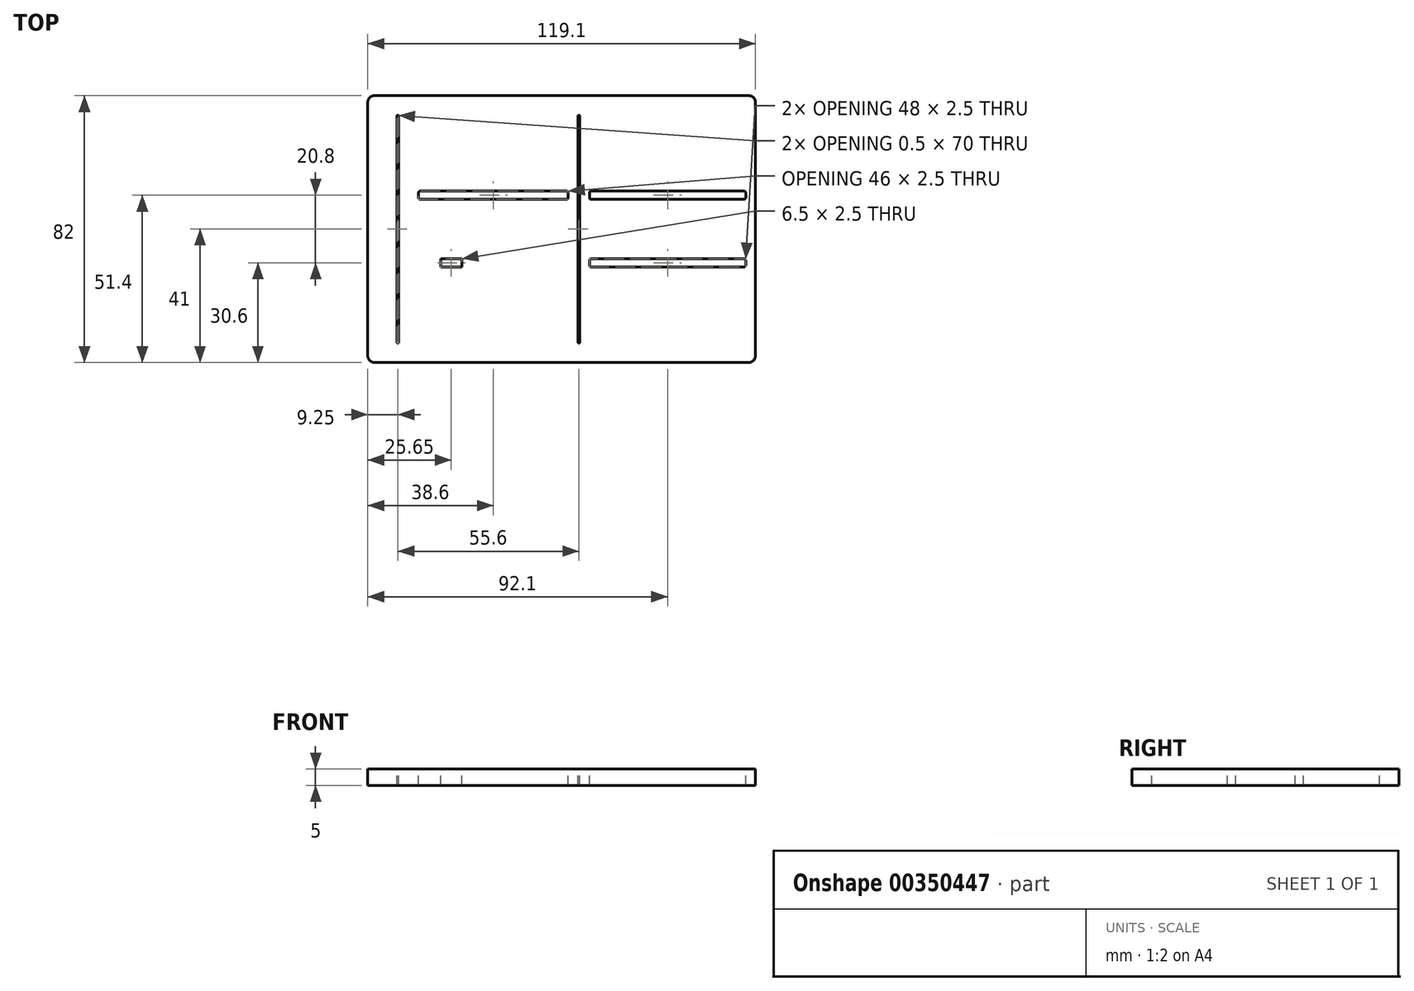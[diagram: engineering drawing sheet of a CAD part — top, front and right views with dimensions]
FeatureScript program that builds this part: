
annotation { "Feature Type Name" : "Feature", "Feature Type Description" : "" }
export const myFeature = defineFeature(function(context is Context, id is Id, definition is map)
    precondition{}
    {
        {
            var Q0;
            Q0=qCreatedBy(makeId("Top.planeOp"),FACE);
            var sketch = newSketch(context, id + "F0", { "sketchPlane" : qUnion([Q0])});
            skLineSegment(sketch, "E0.bottom", {"start": v(0, 0) * mm, "end": v(119.1, 0) * mm});
            skLineSegment(sketch, "E0.top", {"start": v(0, 82) * mm, "end": v(119.1, 82) * mm});
            skLineSegment(sketch, "E0.left", {"start": v(0, 0) * mm, "end": v(0, 82) * mm});
            skLineSegment(sketch, "E0.right", {"start": v(119.1, 0) * mm, "end": v(119.1, 82) * mm});
            skSolve(sketch);
        }
        {
            var Q0;
            Q0=qSketchRegion(id+"F0",true);
            extrude(context, id + "F1", {"entities" : qUnion([Q0]), "depth" : 5 * mm});
        }
        {
            var Q0;
            Q0=makeQuery(id+"F1.opExtrude","CAP_FACE",FACE,{"disambiguationData":[OSD([sQuery(id+"F0.wireOp",EDGE,"E0.bottom"),sQuery(id+"F0.wireOp",EDGE,"E0.top"),sQuery(id+"F0.wireOp",EDGE,"E0.left"),sQuery(id+"F0.wireOp",EDGE,"E0.right")])],"isStart":false});
            var sketch = newSketch(context, id + "F2", { "sketchPlane" : qUnion([Q0])});
            skLineSegment(sketch, "E1", {"start": v(64.6, 25) * mm, "end": v(64.6, 76) * mm});
            skLineSegment(sketch, "E2", {"start": v(64.6, 25) * mm, "end": v(64.6, 6) * mm});
            skLineSegment(sketch, "E3", {"start": v(64.6, 76) * mm, "end": v(65.1, 76) * mm});
            skLineSegment(sketch, "E4", {"start": v(65.1, 76) * mm, "end": v(65.1, 6) * mm});
            skLineSegment(sketch, "E5", {"start": v(65.1, 6) * mm, "end": v(64.6, 6) * mm});
            skSolve(sketch);
        }
        {
            var Q0;
            Q0=qSketchRegion(id+"F2",true);
            extrude(context, id + "F3", {"entities" : qUnion([Q0]), "operationType" : NewBodyOperationType.REMOVE, "oppositeDirection" : true, "depth" : 63.1 * mm});
        }
        {
            var Q0;
            Q0=makeQuery(id+"F1.opExtrude","CAP_FACE",FACE,{"disambiguationData":[OSD([sQuery(id+"F0.wireOp",EDGE,"E0.bottom"),sQuery(id+"F0.wireOp",EDGE,"E0.top"),sQuery(id+"F0.wireOp",EDGE,"E0.left"),sQuery(id+"F0.wireOp",EDGE,"E0.right")])],"isStart":false});
            var sketch = newSketch(context, id + "F4", { "sketchPlane" : qUnion([Q0])});
            skLineSegment(sketch, "E6", {"start": v(38.92, 50.15) * mm, "end": v(61.6, 50.15) * mm});
            skLineSegment(sketch, "E7", {"start": v(38.92, 50.15) * mm, "end": v(38.92, 31.85) * mm});
            skPoint(sketch, "E7.endSnap0", {"position": v(38.92, 41) * mm});
            skLineSegment(sketch, "E8", {"start": v(38.92, 50.15) * mm, "end": v(15.6, 50.15) * mm});
            skLineSegment(sketch, "E9", {"start": v(15.6, 31.85) * mm, "end": v(61.6, 31.85) * mm});
            skLineSegment(sketch, "E10.bottom", {"start": v(15.6, 50.15) * mm, "end": v(61.6, 50.15) * mm});
            skLineSegment(sketch, "E10.top", {"start": v(15.6, 52.65) * mm, "end": v(61.6, 52.65) * mm});
            skLineSegment(sketch, "E10.left", {"start": v(15.6, 50.15) * mm, "end": v(15.6, 52.65) * mm});
            skLineSegment(sketch, "E10.right", {"start": v(61.6, 50.15) * mm, "end": v(61.6, 52.65) * mm});
            skLineSegment(sketch, "E11.top", {"start": v(15.6, 29.35) * mm, "end": v(61.6, 29.35) * mm});
            skLineSegment(sketch, "E11.left", {"start": v(15.6, 31.85) * mm, "end": v(15.6, 29.35) * mm});
            skLineSegment(sketch, "E11.right", {"start": v(61.6, 31.85) * mm, "end": v(61.6, 29.35) * mm});
            skLineSegment(sketch, "E12.bottom", {"start": v(38.92, 31.85) * mm, "end": v(48.1, 31.85) * mm});
            skLineSegment(sketch, "E12.top", {"start": v(38, 29.35) * mm, "end": v(48.1, 29.35) * mm});
            skLineSegment(sketch, "E12.right", {"start": v(48.1, 31.85) * mm, "end": v(48.1, 29.35) * mm});
            skLineSegment(sketch, "E13.bottom", {"start": v(54.6, 31.85) * mm, "end": v(61.6, 31.85) * mm});
            skLineSegment(sketch, "E13.top", {"start": v(54.6, 29.35) * mm, "end": v(61.6, 29.35) * mm});
            skLineSegment(sketch, "E13.left", {"start": v(54.6, 31.85) * mm, "end": v(54.6, 29.35) * mm});
            skLineSegment(sketch, "E14.bottom", {"start": v(15.6, 31.85) * mm, "end": v(22.4, 31.85) * mm});
            skLineSegment(sketch, "E14.top", {"start": v(15.6, 29.35) * mm, "end": v(22.4, 29.35) * mm});
            skLineSegment(sketch, "E14.right", {"start": v(22.4, 31.85) * mm, "end": v(22.4, 29.35) * mm});
            skLineSegment(sketch, "E15.bottom", {"start": v(28.9, 31.85) * mm, "end": v(35.7, 31.85) * mm});
            skLineSegment(sketch, "E15.top", {"start": v(28.9, 29.35) * mm, "end": v(35.7, 29.35) * mm});
            skLineSegment(sketch, "E15.left", {"start": v(28.9, 31.85) * mm, "end": v(28.9, 29.35) * mm});
            skLineSegment(sketch, "E15.right", {"start": v(35.7, 31.85) * mm, "end": v(35.7, 29.35) * mm});
            skLineSegment(sketch, "E16", {"start": v(48.1, 31.85) * mm, "end": v(41.1, 31.85) * mm});
            skLineSegment(sketch, "E17", {"start": v(41.1, 29.35) * mm, "end": v(41.1, 31.85) * mm});
            skLineSegment(sketch, "E18", {"start": v(22.4, 50.15) * mm, "end": v(22.4, 52.65) * mm});
            skLineSegment(sketch, "E19", {"start": v(28.9, 50.15) * mm, "end": v(28.9, 52.65) * mm});
            skLineSegment(sketch, "E20", {"start": v(35.7, 29.35) * mm, "end": v(35.7, 31.85) * mm});
            skLineSegment(sketch, "E21", {"start": v(48.1, 29.35) * mm, "end": v(48.1, 31.85) * mm});
            skLineSegment(sketch, "E22", {"start": v(54.6, 29.35) * mm, "end": v(54.6, 31.85) * mm});
            skLineSegment(sketch, "E23.trimOffspring", {"start": v(35.7, 50.15) * mm, "end": v(35.7, 52.65) * mm});
            skLineSegment(sketch, "E24.trimOffspring", {"start": v(41.1, 50.15) * mm, "end": v(41.1, 52.65) * mm});
            skLineSegment(sketch, "E25.trimOffspring", {"start": v(48.1, 50.15) * mm, "end": v(48.1, 52.65) * mm});
            skLineSegment(sketch, "E26.trimOffspring", {"start": v(54.6, 50.15) * mm, "end": v(54.6, 52.65) * mm});
            skLineSegment(sketch, "E27", {"start": v(38.92, 41) * mm, "end": v(38.92, 31.85) * mm});
            skSolve(sketch);
        }
        {
            var Q0;
            {var subQ0=sQuery(id+"F4.wireOp",EDGE,"E19");Q0=makeQuery(id+"F4.imprint","IMPRINT",FACE,{"disambiguationData":[TD([[makeQuery(id+"F4.imprint","IMPRINT",EDGE,{"derivedFrom":subQ0}),-1.0]])]});}
            var Q1;
            {var subQ0=sQuery(id+"F4.wireOp",EDGE,"E23.trimOffspring");Q1=makeQuery(id+"F4.imprint","IMPRINT",FACE,{"disambiguationData":[TD([[makeQuery(id+"F4.imprint","IMPRINT",EDGE,{"derivedFrom":subQ0}),-1.0]])]});}
            var Q2;
            {var subQ0=sQuery(id+"F4.wireOp",EDGE,"E24.trimOffspring");Q2=makeQuery(id+"F4.imprint","IMPRINT",FACE,{"disambiguationData":[TD([[makeQuery(id+"F4.imprint","IMPRINT",EDGE,{"derivedFrom":subQ0}),-1.0]])]});}
            var Q3;
            {var subQ0=sQuery(id+"F4.wireOp",EDGE,"E25.trimOffspring");Q3=makeQuery(id+"F4.imprint","IMPRINT",FACE,{"disambiguationData":[TD([[makeQuery(id+"F4.imprint","IMPRINT",EDGE,{"derivedFrom":subQ0}),-1.0]])]});}
            var Q4;
            {var subQ0=sQuery(id+"F4.wireOp",EDGE,"E10.left");Q4=makeQuery(id+"F4.imprint","IMPRINT",FACE,{"disambiguationData":[TD([[makeQuery(id+"F4.imprint","IMPRINT",EDGE,{"derivedFrom":subQ0}),-1.0]])]});}
            var Q5;
            {var subQ0=sQuery(id+"F4.wireOp",EDGE,"E18");Q5=makeQuery(id+"F4.imprint","IMPRINT",FACE,{"disambiguationData":[TD([[makeQuery(id+"F4.imprint","IMPRINT",EDGE,{"derivedFrom":subQ0}),-1.0]])]});}
            var Q6;
            {var subQ0=sQuery(id+"F4.wireOp",EDGE,"E10.right");Q6=makeQuery(id+"F4.imprint","IMPRINT",FACE,{"disambiguationData":[TD([[makeQuery(id+"F4.imprint","IMPRINT",EDGE,{"derivedFrom":subQ0}),1.0]])]});}
            var Q7;
            Q7=makeQuery(id+"F4.imprint","IMPRINT",FACE,{"disambiguationData":[TD([[makeQuery(id+"F4.imprint","IMPRINT",EDGE,{"derivedFrom":sQuery(id+"F4.wireOp",EDGE,"E16")}),1.0]])]});
            var Q8;
            Q8=makeQuery(id+"F4.imprint","IMPRINT",FACE,{"disambiguationData":[TD([[makeQuery(id+"F4.imprint","IMPRINT",EDGE,{"derivedFrom":sQuery(id+"F4.wireOp",EDGE,"E15.bottom")}),-1.0]])]});
            var Q9;
            Q9=makeQuery(id+"F4.imprint","IMPRINT",FACE,{"disambiguationData":[TD([[makeQuery(id+"F4.imprint","IMPRINT",EDGE,{"derivedFrom":sQuery(id+"F4.wireOp",EDGE,"E13.bottom")}),-1.0]])]});
            var Q10;
            {var subQ5=sQuery(id+"F4.wireOp",EDGE,"E12.bottom");Q10=makeQuery(id+"F4.imprint","IMPRINT",FACE,{"disambiguationData":[TD([[makeQuery(id+"F4.imprint","IMPRINT",EDGE,{"derivedFrom":subQ5}),-1.0]])]});}
            var Q11;
            {var subQ2=sQuery(id+"F4.wireOp",EDGE,"E21");Q11=makeQuery(id+"F4.imprint","IMPRINT",FACE,{"disambiguationData":[TD([[makeQuery(id+"F4.imprint","IMPRINT",EDGE,{"derivedFrom":subQ2}),-1.0]])]});}
            var Q12;
            {var subQ0=sQuery(id+"F4.wireOp",EDGE,"E14.right");Q12=makeQuery(id+"F4.imprint","IMPRINT",FACE,{"disambiguationData":[TD([[makeQuery(id+"F4.imprint","IMPRINT",EDGE,{"derivedFrom":subQ0}),1.0]])]});}
            var Q13;
            Q13=makeQuery(id+"F4.imprint","IMPRINT",FACE,{"disambiguationData":[TD([[makeQuery(id+"F4.imprint","IMPRINT",EDGE,{"derivedFrom":sQuery(id+"F4.wireOp",EDGE,"E14.bottom")}),-1.0]])]});
            extrude(context, id + "F5", {"entities" : qUnion([Q0, Q1, Q2, Q3, Q4, Q5, Q6, Q7, Q8, Q9, Q10, Q11, Q12, Q13]), "operationType" : NewBodyOperationType.REMOVE, "oppositeDirection" : true, "depth" : 53.3 * mm});
        }
        {
            var Q0;
            Q0=makeQuery(id+"F1.opExtrude","CAP_FACE",FACE,{"disambiguationData":[OSD([sQuery(id+"F0.wireOp",EDGE,"E0.bottom"),sQuery(id+"F0.wireOp",EDGE,"E0.top"),sQuery(id+"F0.wireOp",EDGE,"E0.left"),sQuery(id+"F0.wireOp",EDGE,"E0.right")])],"isStart":false});
            var sketch = newSketch(context, id + "F6", { "sketchPlane" : qUnion([Q0])});
            skLineSegment(sketch, "E28", {"start": v(68.1, 52.65) * mm, "end": v(116.1, 52.65) * mm});
            skLineSegment(sketch, "E29", {"start": v(116.1, 52.65) * mm, "end": v(116.1, 50.15) * mm});
            skLineSegment(sketch, "E30", {"start": v(116.1, 50.15) * mm, "end": v(68.1, 50.15) * mm});
            skLineSegment(sketch, "E31", {"start": v(68.1, 50.15) * mm, "end": v(68.1, 52.65) * mm});
            skLineSegment(sketch, "E32", {"start": v(68.1, 31.85) * mm, "end": v(68.1, 29.35) * mm});
            skLineSegment(sketch, "E33", {"start": v(68.1, 29.35) * mm, "end": v(116.1, 29.35) * mm});
            skLineSegment(sketch, "E34", {"start": v(116.1, 29.35) * mm, "end": v(116.1, 31.85) * mm});
            skLineSegment(sketch, "E35", {"start": v(116.1, 31.85) * mm, "end": v(68.1, 31.85) * mm});
            skSolve(sketch);
        }
        {
            var Q0;
            Q0=makeQuery(id+"F6.imprint","IMPRINT",FACE,{"disambiguationData":[TD([[makeQuery(id+"F6.imprint","IMPRINT",EDGE,{"derivedFrom":sQuery(id+"F6.wireOp",EDGE,"E28")}),-1.0]])]});
            var Q1;
            Q1=makeQuery(id+"F6.imprint","IMPRINT",FACE,{"disambiguationData":[TD([[makeQuery(id+"F6.imprint","IMPRINT",EDGE,{"derivedFrom":sQuery(id+"F6.wireOp",EDGE,"E32")}),1.0]])]});
            extrude(context, id + "F7", {"entities" : qUnion([Q0, Q1]), "operationType" : NewBodyOperationType.REMOVE, "oppositeDirection" : true, "depth" : 27.8 * mm});
        }
        {
            var Q0;
            Q0=makeQuery(id+"F1.opExtrude","CAP_FACE",FACE,{"disambiguationData":[OSD([sQuery(id+"F0.wireOp",EDGE,"E0.bottom"),sQuery(id+"F0.wireOp",EDGE,"E0.top"),sQuery(id+"F0.wireOp",EDGE,"E0.left"),sQuery(id+"F0.wireOp",EDGE,"E0.right")])],"isStart":false});
            var sketch = newSketch(context, id + "F8", { "sketchPlane" : qUnion([Q0])});
            skLineSegment(sketch, "E36.bottom", {"start": v(9, 76) * mm, "end": v(9.5, 76) * mm});
            skLineSegment(sketch, "E36.top", {"start": v(9, 6) * mm, "end": v(9.5, 6) * mm});
            skLineSegment(sketch, "E36.left", {"start": v(9, 76) * mm, "end": v(9, 6) * mm});
            skLineSegment(sketch, "E36.right", {"start": v(9.5, 76) * mm, "end": v(9.5, 6) * mm});
            skSolve(sketch);
        }
        {
            var Q0;
            Q0=makeQuery(id+"F8.imprint","IMPRINT",FACE,{"disambiguationData":[TD([[makeQuery(id+"F8.imprint","IMPRINT",EDGE,{"derivedFrom":sQuery(id+"F8.wireOp",EDGE,"E36.bottom")}),-1.0]])]});
            extrude(context, id + "F9", {"entities" : qUnion([Q0]), "operationType" : NewBodyOperationType.REMOVE, "oppositeDirection" : true, "depth" : 25 * mm});
        }
        {
            var Q0;
            Q0=makeQuery(id+"F1.opExtrude","SWEPT_EDGE",EDGE,{"disambiguationData":[OSD([sQuery(id+"F0.wireOp",EDGE,"E0.bottom"),sQuery(id+"F0.wireOp",EDGE,"E0.right")])]});
            var Q1;
            Q1=makeQuery(id+"F1.opExtrude","SWEPT_EDGE",EDGE,{"disambiguationData":[OSD([sQuery(id+"F0.wireOp",EDGE,"E0.bottom"),sQuery(id+"F0.wireOp",EDGE,"E0.left")])]});
            var Q2;
            Q2=makeQuery(id+"F1.opExtrude","SWEPT_EDGE",EDGE,{"disambiguationData":[OSD([sQuery(id+"F0.wireOp",EDGE,"E0.top"),sQuery(id+"F0.wireOp",EDGE,"E0.right")])]});
            var Q3;
            Q3=makeQuery(id+"F1.opExtrude","SWEPT_EDGE",EDGE,{"disambiguationData":[OSD([sQuery(id+"F0.wireOp",EDGE,"E0.top"),sQuery(id+"F0.wireOp",EDGE,"E0.left")])]});
            fillet(context, id + "F10", {"entities" : qUnion([Q0, Q1, Q2, Q3]), "radius" : 2 * mm, "tangentPropagation" : true, "allowEdgeOverflow" : false});
        }
        {
            var Q0;
            Q0=makeQuery(id+"F5.boolean.opBoolean","COPY",EDGE,{"derivedFrom":makeQuery(id+"F5.opExtrude","SWEPT_EDGE",EDGE,{"disambiguationData":[OSD([sQuery(id+"F4.wireOp",EDGE,"E10.top"),sQuery(id+"F4.wireOp",EDGE,"E10.left")])]})});
            var Q1;
            Q1=makeQuery(id+"F5.boolean.opBoolean","COPY",EDGE,{"derivedFrom":makeQuery(id+"F5.opExtrude","SWEPT_EDGE",EDGE,{"disambiguationData":[OSD([sQuery(id+"F4.wireOp",EDGE,"E10.bottom"),sQuery(id+"F4.wireOp",EDGE,"E10.left")])]})});
            var Q2;
            Q2=makeQuery(id+"F5.boolean.opBoolean","COPY",EDGE,{"derivedFrom":makeQuery(id+"F5.opExtrude","SWEPT_EDGE",EDGE,{"disambiguationData":[OSD([sQuery(id+"F4.wireOp",EDGE,"E10.top"),sQuery(id+"F4.wireOp",EDGE,"E10.right")])]})});
            var Q3;
            Q3=makeQuery(id+"F5.boolean.opBoolean","COPY",EDGE,{"derivedFrom":makeQuery(id+"F5.opExtrude","SWEPT_EDGE",EDGE,{"disambiguationData":[OSD([sQuery(id+"F4.wireOp",EDGE,"E10.bottom"),sQuery(id+"F4.wireOp",EDGE,"E10.right")])]})});
            var Q4;
            Q4=makeQuery(id+"F7.boolean.opBoolean","COPY",EDGE,{"derivedFrom":makeQuery(id+"F7.opExtrude","SWEPT_EDGE",EDGE,{"disambiguationData":[OSD([sQuery(id+"F6.wireOp",EDGE,"E28"),sQuery(id+"F6.wireOp",EDGE,"E31")])]})});
            var Q5;
            Q5=makeQuery(id+"F7.boolean.opBoolean","COPY",EDGE,{"derivedFrom":makeQuery(id+"F7.opExtrude","SWEPT_EDGE",EDGE,{"disambiguationData":[OSD([sQuery(id+"F6.wireOp",EDGE,"E30"),sQuery(id+"F6.wireOp",EDGE,"E31")])]})});
            var Q6;
            Q6=makeQuery(id+"F7.boolean.opBoolean","COPY",EDGE,{"derivedFrom":makeQuery(id+"F7.opExtrude","SWEPT_EDGE",EDGE,{"disambiguationData":[OSD([sQuery(id+"F6.wireOp",EDGE,"E28"),sQuery(id+"F6.wireOp",EDGE,"E29")])]})});
            var Q7;
            Q7=makeQuery(id+"F7.boolean.opBoolean","COPY",EDGE,{"derivedFrom":makeQuery(id+"F7.opExtrude","SWEPT_EDGE",EDGE,{"disambiguationData":[OSD([sQuery(id+"F6.wireOp",EDGE,"E29"),sQuery(id+"F6.wireOp",EDGE,"E30")])]})});
            var Q8;
            Q8=makeQuery(id+"F7.boolean.opBoolean","COPY",EDGE,{"derivedFrom":makeQuery(id+"F7.opExtrude","SWEPT_EDGE",EDGE,{"disambiguationData":[OSD([sQuery(id+"F6.wireOp",EDGE,"E33"),sQuery(id+"F6.wireOp",EDGE,"E34")])]})});
            var Q9;
            Q9=makeQuery(id+"F7.boolean.opBoolean","COPY",EDGE,{"derivedFrom":makeQuery(id+"F7.opExtrude","SWEPT_EDGE",EDGE,{"disambiguationData":[OSD([sQuery(id+"F6.wireOp",EDGE,"E34"),sQuery(id+"F6.wireOp",EDGE,"E35")])]})});
            var Q10;
            Q10=makeQuery(id+"F7.boolean.opBoolean","COPY",EDGE,{"derivedFrom":makeQuery(id+"F7.opExtrude","SWEPT_EDGE",EDGE,{"disambiguationData":[OSD([sQuery(id+"F6.wireOp",EDGE,"E32"),sQuery(id+"F6.wireOp",EDGE,"E35")])]})});
            var Q11;
            Q11=makeQuery(id+"F7.boolean.opBoolean","COPY",EDGE,{"derivedFrom":makeQuery(id+"F7.opExtrude","SWEPT_EDGE",EDGE,{"disambiguationData":[OSD([sQuery(id+"F6.wireOp",EDGE,"E32"),sQuery(id+"F6.wireOp",EDGE,"E33")])]})});
            var Q12;
            Q12=makeQuery(id+"F5.boolean.opBoolean","COPY",EDGE,{"derivedFrom":makeQuery(id+"F5.opExtrude","SWEPT_EDGE",EDGE,{"disambiguationData":[OSD([sQuery(id+"F4.wireOp",EDGE,"E14.top"),sQuery(id+"F4.wireOp",EDGE,"E11.left")])]})});
            var Q13;
            Q13=makeQuery(id+"F5.boolean.opBoolean","COPY",EDGE,{"derivedFrom":makeQuery(id+"F5.opExtrude","SWEPT_EDGE",EDGE,{"disambiguationData":[OSD([sQuery(id+"F4.wireOp",EDGE,"E14.bottom"),sQuery(id+"F4.wireOp",EDGE,"E11.left")])]})});
            var Q14;
            Q14=makeQuery(id+"F5.boolean.opBoolean","COPY",EDGE,{"derivedFrom":makeQuery(id+"F5.opExtrude","SWEPT_EDGE",EDGE,{"disambiguationData":[OSD([sQuery(id+"F4.wireOp",EDGE,"E13.top"),sQuery(id+"F4.wireOp",EDGE,"E11.right")])]})});
            var Q15;
            Q15=makeQuery(id+"F5.boolean.opBoolean","COPY",EDGE,{"derivedFrom":makeQuery(id+"F5.opExtrude","SWEPT_EDGE",EDGE,{"disambiguationData":[OSD([sQuery(id+"F4.wireOp",EDGE,"E13.bottom"),sQuery(id+"F4.wireOp",EDGE,"E11.right")])]})});
            fillet(context, id + "F11", {"entities" : qUnion([Q0, Q1, Q2, Q3, Q4, Q5, Q6, Q7, Q8, Q9, Q10, Q11, Q12, Q13, Q14, Q15]), "radius" : .5 * mm, "tangentPropagation" : true, "allowEdgeOverflow" : false});
        }
        {
            var Q0;
            Q0=makeQuery(id+"F3.boolean.opBoolean","COPY",EDGE,{"derivedFrom":makeQuery(id+"F3.opExtrude","SWEPT_EDGE",EDGE,{"disambiguationData":[OSD([sQuery(id+"F2.wireOp",EDGE,"E2"),sQuery(id+"F2.wireOp",EDGE,"E5")])]})});
            var Q1;
            Q1=makeQuery(id+"F3.boolean.opBoolean","COPY",EDGE,{"derivedFrom":makeQuery(id+"F3.opExtrude","SWEPT_EDGE",EDGE,{"disambiguationData":[OSD([sQuery(id+"F2.wireOp",EDGE,"E4"),sQuery(id+"F2.wireOp",EDGE,"E5")])]})});
            var Q2;
            Q2=makeQuery(id+"F3.boolean.opBoolean","COPY",EDGE,{"derivedFrom":makeQuery(id+"F3.opExtrude","SWEPT_EDGE",EDGE,{"disambiguationData":[OSD([sQuery(id+"F2.wireOp",EDGE,"E1"),sQuery(id+"F2.wireOp",EDGE,"E3")])]})});
            var Q3;
            Q3=makeQuery(id+"F3.boolean.opBoolean","COPY",EDGE,{"derivedFrom":makeQuery(id+"F3.opExtrude","SWEPT_EDGE",EDGE,{"disambiguationData":[OSD([sQuery(id+"F2.wireOp",EDGE,"E3"),sQuery(id+"F2.wireOp",EDGE,"E4")])]})});
            var Q4;
            Q4=makeQuery(id+"F9.boolean.opBoolean","COPY",EDGE,{"derivedFrom":makeQuery(id+"F9.opExtrude","SWEPT_EDGE",EDGE,{"disambiguationData":[OSD([sQuery(id+"F8.wireOp",EDGE,"E36.bottom"),sQuery(id+"F8.wireOp",EDGE,"E36.right")])]})});
            var Q5;
            Q5=makeQuery(id+"F9.boolean.opBoolean","COPY",EDGE,{"derivedFrom":makeQuery(id+"F9.opExtrude","SWEPT_EDGE",EDGE,{"disambiguationData":[OSD([sQuery(id+"F8.wireOp",EDGE,"E36.bottom"),sQuery(id+"F8.wireOp",EDGE,"E36.left")])]})});
            var Q6;
            Q6=makeQuery(id+"F9.boolean.opBoolean","COPY",EDGE,{"derivedFrom":makeQuery(id+"F9.opExtrude","SWEPT_EDGE",EDGE,{"disambiguationData":[OSD([sQuery(id+"F8.wireOp",EDGE,"E36.top"),sQuery(id+"F8.wireOp",EDGE,"E36.left")])]})});
            var Q7;
            Q7=makeQuery(id+"F9.boolean.opBoolean","COPY",EDGE,{"derivedFrom":makeQuery(id+"F9.opExtrude","SWEPT_EDGE",EDGE,{"disambiguationData":[OSD([sQuery(id+"F8.wireOp",EDGE,"E36.top"),sQuery(id+"F8.wireOp",EDGE,"E36.right")])]})});
            fillet(context, id + "F12", {"entities" : qUnion([Q0, Q1, Q2, Q3, Q4, Q5, Q6, Q7]), "radius" : .1 * mm, "tangentPropagation" : true, "allowEdgeOverflow" : false});
        }
    });
